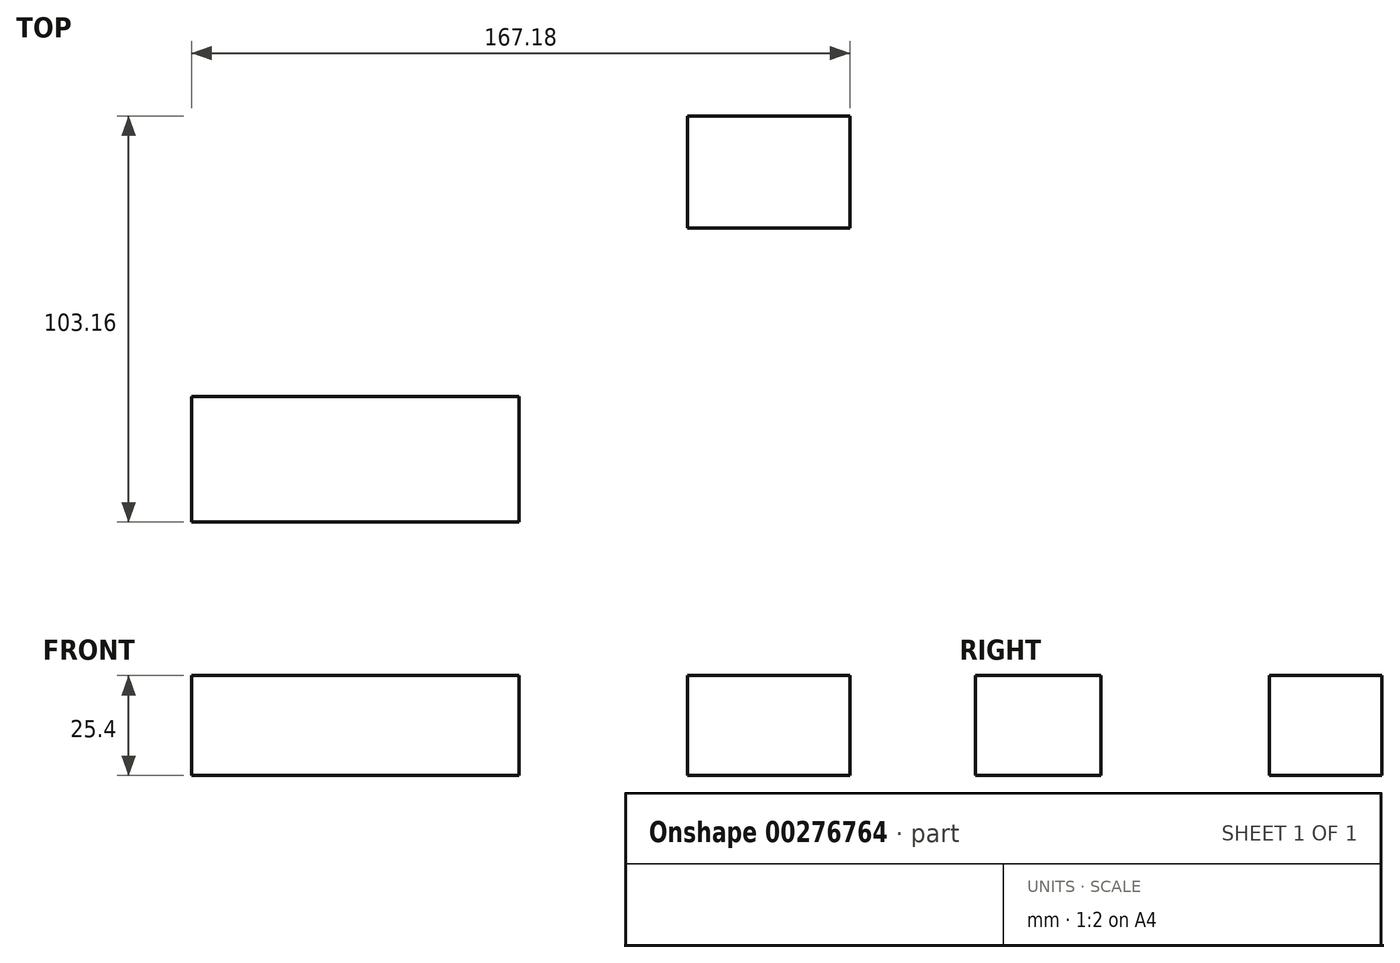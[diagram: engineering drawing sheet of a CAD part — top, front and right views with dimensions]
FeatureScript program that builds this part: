
annotation { "Feature Type Name" : "Feature", "Feature Type Description" : "" }
export const myFeature = defineFeature(function(context is Context, id is Id, definition is map)
    precondition{}
    {
        {
            var Q0;
            Q0=qCreatedBy(makeId("Top.planeOp"),FACE);
            var sketch = newSketch(context, id + "F0", { "sketchPlane" : qUnion([Q0])});
            skLineSegment(sketch, "E0.bottom", {"start": v(-41.57, 15.93) * mm, "end": v(41.57, 15.93) * mm});
            skLineSegment(sketch, "E0.top", {"start": v(-41.57, -15.93) * mm, "end": v(41.57, -15.93) * mm});
            skLineSegment(sketch, "E0.left", {"start": v(-41.57, 15.93) * mm, "end": v(-41.57, -15.93) * mm});
            skLineSegment(sketch, "E0.right", {"start": v(41.57, 15.93) * mm, "end": v(41.57, -15.93) * mm});
            skPoint(sketch, "E0.middle", {"position": v(0, 0) * mm});
            skLineSegment(sketch, "E1.bottom", {"start": v(84.34, 58.7) * mm, "end": v(125.6, 58.7) * mm});
            skLineSegment(sketch, "E1.top", {"start": v(84.34, 87.23) * mm, "end": v(125.6, 87.23) * mm});
            skLineSegment(sketch, "E1.left", {"start": v(84.34, 58.7) * mm, "end": v(84.34, 87.23) * mm});
            skLineSegment(sketch, "E1.right", {"start": v(125.6, 58.7) * mm, "end": v(125.6, 87.23) * mm});
            skPoint(sketch, "E1.middle", {"position": v(104.98, 72.97) * mm});
            skLineSegment(sketch, "E2", {"start": v(41.57, 15.93) * mm, "end": v(41.57, 58.7) * mm});
            skArc(sketch, "E3", {"start": v(41.57, 58.7) * mm, "mid": v(45.32, 67.78) * mm, "end": v(54.39, 71.53) * mm});
            skLineSegment(sketch, "E4", {"start": v(54.39, 71.53) * mm, "end": v(101.73, 71.53) * mm});
            skSolve(sketch);
        }
        {
            var Q0;
            Q0 = qSketchRegion(id + "F0", true);
            extrude(context, id + "F1", {"entities" : qUnion([Q0]), "depth" : 25.4 * mm});
        }
    });
